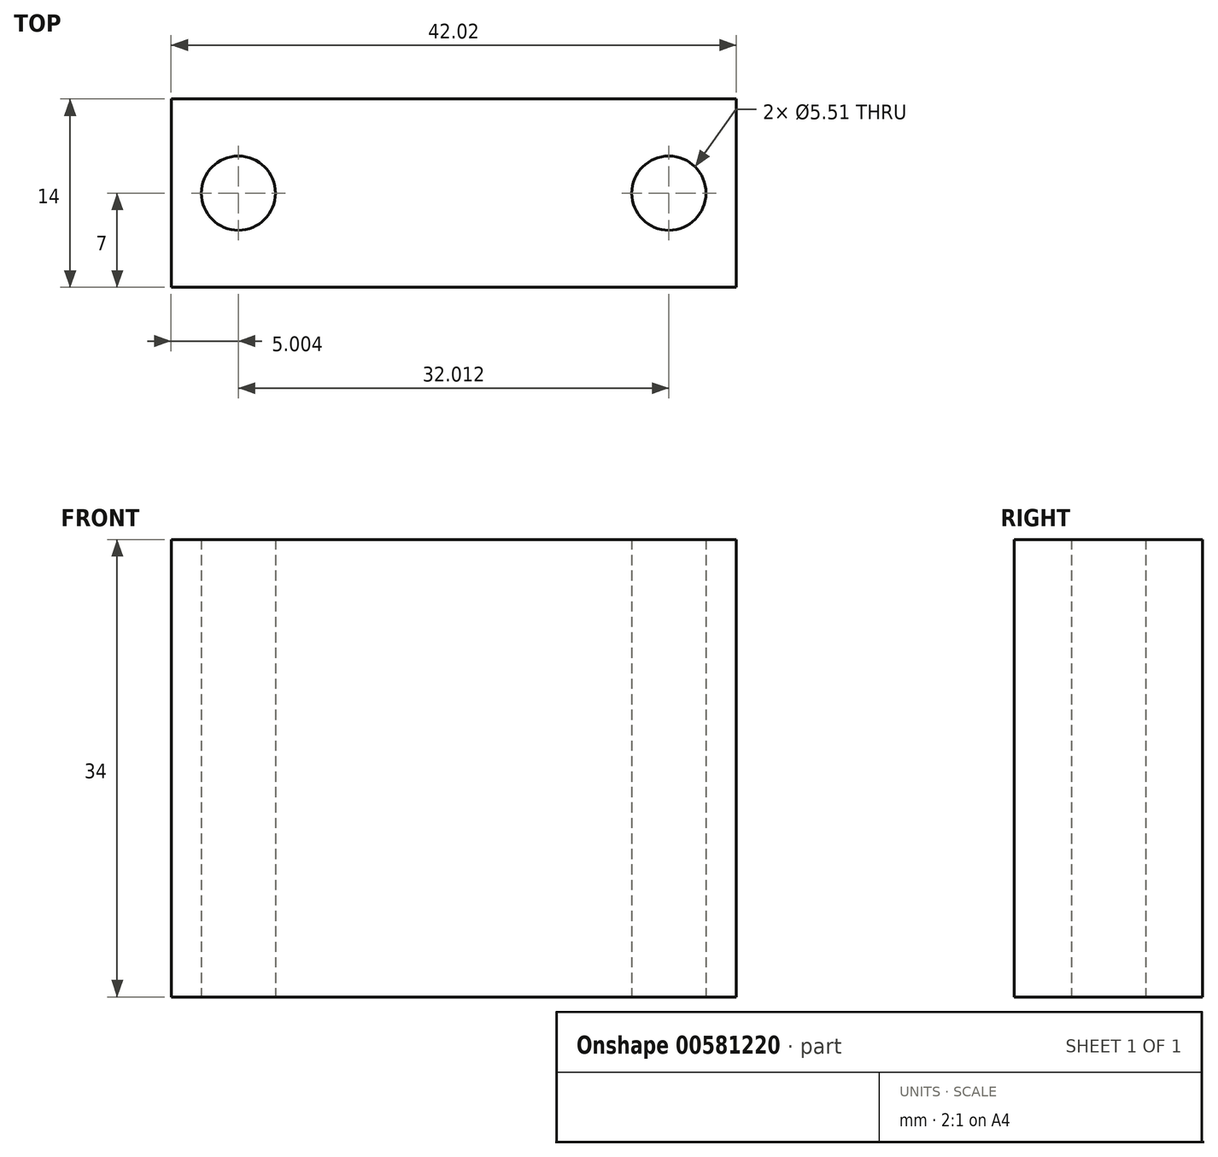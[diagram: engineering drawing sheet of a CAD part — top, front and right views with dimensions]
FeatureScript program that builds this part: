
annotation { "Feature Type Name" : "Feature", "Feature Type Description" : "" }
export const myFeature = defineFeature(function(context is Context, id is Id, definition is map)
    precondition{}
    {
        {
            var Q0;
            Q0=qCreatedBy(makeId("Top.planeOp"),FACE);
            var sketch = newSketch(context, id + "F0", { "sketchPlane" : qUnion([Q0])});
            skLineSegment(sketch, "E0.bottom", {"start": v(21, 7) * mm, "end": v(-21, 7) * mm});
            skLineSegment(sketch, "E0.top", {"start": v(21, -7) * mm, "end": v(-21, -7) * mm});
            skLineSegment(sketch, "E0.left", {"start": v(21, 7) * mm, "end": v(21, -7) * mm});
            skLineSegment(sketch, "E0.right", {"start": v(-21, 7) * mm, "end": v(-21, -7) * mm});
            skPoint(sketch, "E0.middle", {"position": v(0, 0) * mm});
            skCircle(sketch, "E1", {"center": v(16, 0) * mm, "radius": 2.76 * mm});
            skCircle(sketch, "E2.MirrorC", {"center": v(-16, 0) * mm, "radius": 2.76 * mm});
            skSolve(sketch);
        }
        {
            var Q0;
            Q0 = qSketchRegion(id + "F0", true);
            extrude(context, id + "F1", {"entities" : qUnion([Q0]), "depth" : 34 * mm, "offsetDistance" : 25.4 * mm});
        }
    });
